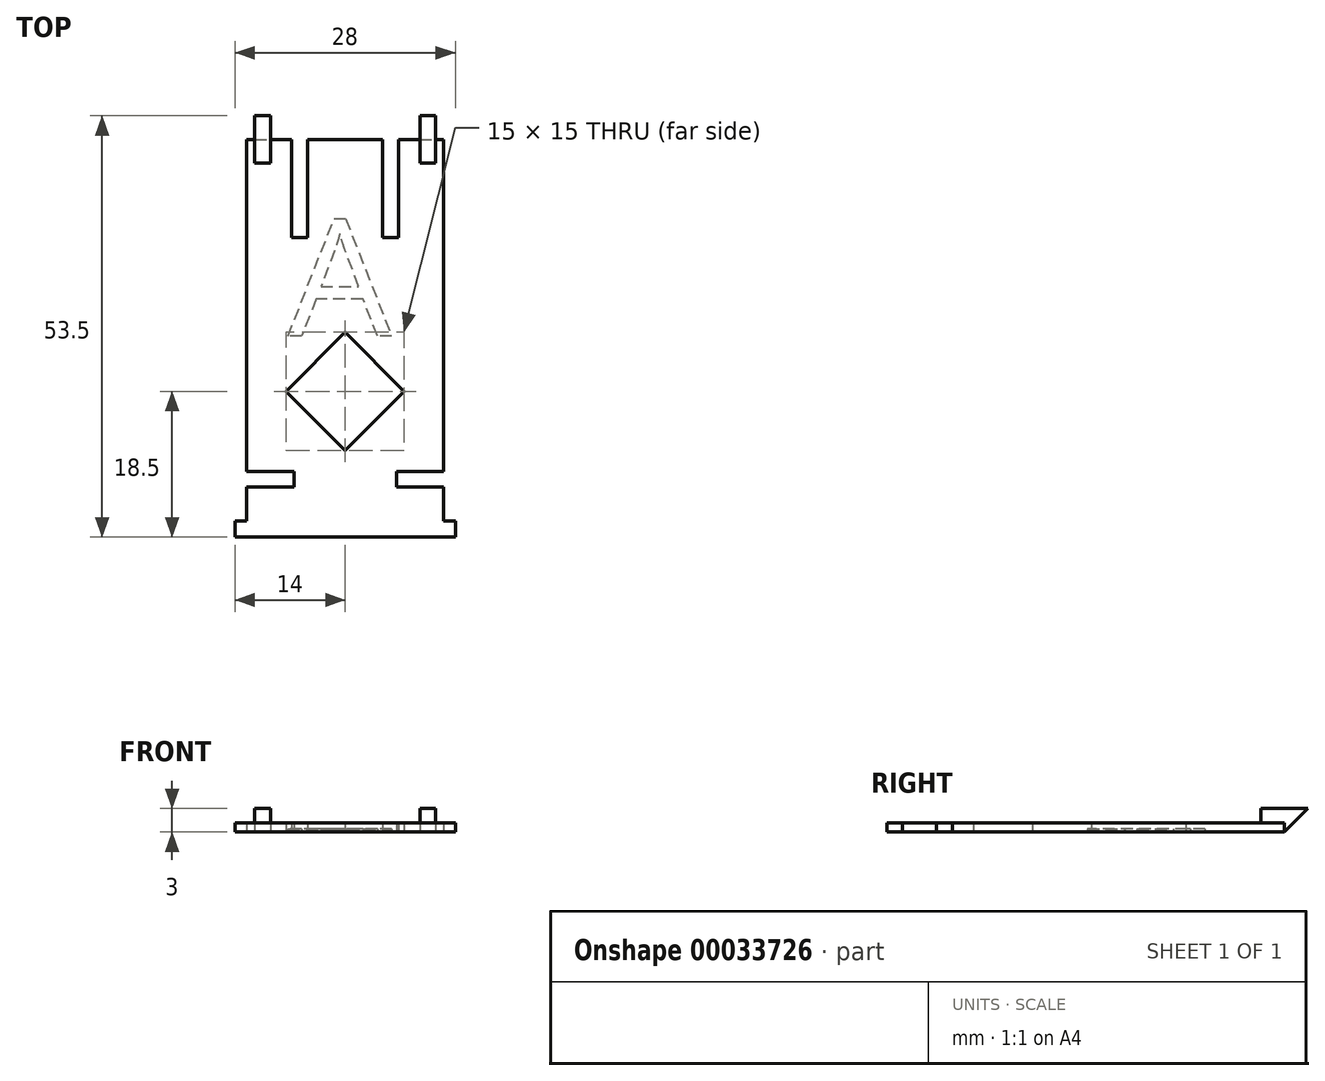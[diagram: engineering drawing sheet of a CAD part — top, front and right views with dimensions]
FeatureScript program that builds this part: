
annotation { "Feature Type Name" : "Feature", "Feature Type Description" : "" }
export const myFeature = defineFeature(function(context is Context, id is Id, definition is map)
    precondition{}
    {
        {
            var Q0;
            Q0=qCreatedBy(makeId("Top.planeOp"),FACE);
            var sketch = newSketch(context, id + "F0", { "sketchPlane" : qUnion([Q0])});
            skLineSegment(sketch, "E0.bottom", {"start": v(-12.5, 25.25) * mm, "end": v(12.5, 25.25) * mm});
            skLineSegment(sketch, "E0.top", {"start": v(-12.5, -25.25) * mm, "end": v(12.5, -25.25) * mm});
            skLineSegment(sketch, "E0.left", {"start": v(-12.5, 25.25) * mm, "end": v(-12.5, -25.25) * mm});
            skLineSegment(sketch, "E0.right", {"start": v(12.5, 25.25) * mm, "end": v(12.5, -25.25) * mm});
            skPoint(sketch, "E0.middle", {"position": v(0, 0) * mm});
            skLineSegment(sketch, "E1.bottom", {"start": v(-11.5, 28.25) * mm, "end": v(-9.5, 28.25) * mm});
            skLineSegment(sketch, "E1.top", {"start": v(-11.5, 22.25) * mm, "end": v(-9.5, 22.25) * mm});
            skLineSegment(sketch, "E1.left", {"start": v(-11.5, 28.25) * mm, "end": v(-11.5, 22.25) * mm});
            skLineSegment(sketch, "E1.right", {"start": v(-9.5, 28.25) * mm, "end": v(-9.5, 22.25) * mm});
            skPoint(sketch, "E1.middle", {"position": v(-10.5, 25.25) * mm});
            skLineSegment(sketch, "E2.MirrorCS", {"start": v(9.5, 28.25) * mm, "end": v(9.5, 22.25) * mm});
            skLineSegment(sketch, "E3.MirrorCS", {"start": v(11.5, 28.25) * mm, "end": v(9.5, 28.25) * mm});
            skLineSegment(sketch, "E4.MirrorCS", {"start": v(11.5, 28.25) * mm, "end": v(11.5, 22.25) * mm});
            skLineSegment(sketch, "E5.MirrorCS", {"start": v(11.5, 22.25) * mm, "end": v(9.5, 22.25) * mm});
            skPoint(sketch, "E6.MirrorP", {"position": v(10.5, 25.25) * mm});
            skLineSegment(sketch, "E7.bottom", {"start": v(-6.78, 12.75) * mm, "end": v(-4.78, 12.75) * mm});
            skLineSegment(sketch, "E7.top", {"start": v(-6.78, 37.75) * mm, "end": v(-4.78, 37.75) * mm});
            skLineSegment(sketch, "E7.left", {"start": v(-6.78, 12.75) * mm, "end": v(-6.78, 37.75) * mm});
            skLineSegment(sketch, "E7.right", {"start": v(-4.78, 12.75) * mm, "end": v(-4.78, 37.75) * mm});
            skPoint(sketch, "E7.middle", {"position": v(-5.78, 25.25) * mm});
            skLineSegment(sketch, "E8.MirrorCS", {"start": v(6.78, 12.75) * mm, "end": v(6.78, 37.75) * mm});
            skLineSegment(sketch, "E9.MirrorCS", {"start": v(4.78, 12.75) * mm, "end": v(4.78, 37.75) * mm});
            skLineSegment(sketch, "E10.MirrorCS", {"start": v(6.78, 37.75) * mm, "end": v(4.78, 37.75) * mm});
            skLineSegment(sketch, "E11.MirrorCS", {"start": v(6.78, 12.75) * mm, "end": v(4.78, 12.75) * mm});
            skCircle(sketch, "E12.cCircle", {"center": v(0, -6.75) * mm, "radius": 7.5 * mm, "construction": true});
            skLineSegment(sketch, "E12.0", {"start": v(0, 0.75) * mm, "end": v(7.5, -6.75) * mm});
            skLineSegment(sketch, "E12.1", {"start": v(7.5, -6.75) * mm, "end": v(0, -14.25) * mm});
            skLineSegment(sketch, "E12.2", {"start": v(0, -14.25) * mm, "end": v(-7.5, -6.75) * mm});
            skLineSegment(sketch, "E12.3", {"start": v(-7.5, -6.75) * mm, "end": v(0, 0.75) * mm});
            skLineSegment(sketch, "E13.bottom", {"start": v(-12.5, -25.25) * mm, "end": v(-14, -25.25) * mm});
            skLineSegment(sketch, "E13.top", {"start": v(-12.5, -23.25) * mm, "end": v(-14, -23.25) * mm});
            skLineSegment(sketch, "E13.left", {"start": v(-12.5, -25.25) * mm, "end": v(-12.5, -23.25) * mm});
            skLineSegment(sketch, "E13.right", {"start": v(-14, -25.25) * mm, "end": v(-14, -23.25) * mm});
            skLineSegment(sketch, "E14.MirrorCS", {"start": v(14, -25.25) * mm, "end": v(14, -23.25) * mm});
            skLineSegment(sketch, "E15.MirrorCS", {"start": v(12.5, -23.25) * mm, "end": v(14, -23.25) * mm});
            skLineSegment(sketch, "E16.MirrorCS", {"start": v(12.5, -25.25) * mm, "end": v(14, -25.25) * mm});
            skLineSegment(sketch, "E17.bottom", {"start": v(-18.5, -16.93) * mm, "end": v(-6.5, -16.93) * mm});
            skLineSegment(sketch, "E17.top", {"start": v(-18.5, -18.93) * mm, "end": v(-6.5, -18.93) * mm});
            skLineSegment(sketch, "E17.left", {"start": v(-18.5, -16.93) * mm, "end": v(-18.5, -18.93) * mm});
            skLineSegment(sketch, "E17.right", {"start": v(-6.5, -16.93) * mm, "end": v(-6.5, -18.93) * mm});
            skPoint(sketch, "E17.middle", {"position": v(-12.5, -17.93) * mm});
            skLineSegment(sketch, "E18.MirrorCS", {"start": v(18.5, -16.93) * mm, "end": v(6.5, -16.93) * mm});
            skLineSegment(sketch, "E19.MirrorCS", {"start": v(18.5, -18.93) * mm, "end": v(6.5, -18.93) * mm});
            skLineSegment(sketch, "E20.MirrorCS", {"start": v(6.5, -16.93) * mm, "end": v(6.5, -18.93) * mm});
            skLineSegment(sketch, "E21.MirrorCS", {"start": v(18.5, -16.93) * mm, "end": v(18.5, -18.93) * mm});
            skText(sketch, "E22", { "text": "A", "fontName": "OpenSans-Regular.ttf"});
            const initialGuessF0  = {"E22": [-0.00727, 0.00025, 1, 0, 0.015]};
            skSetInitialGuess(sketch, initialGuessF0);
            skSolve(sketch);
        }
        {
            var Q0;
            {var subQ11=sQuery(id+"F0.wireOp",EDGE,"E0.top");Q0=makeQuery(id+"F0.imprint","IMPRINT",FACE,{"disambiguationData":[TD([[makeQuery(id+"F0.imprint","IMPRINT",EDGE,{"derivedFrom":subQ11}),1.0]])]});}
            var Q1;
            {var subQ0=sQuery(id+"F0.wireOp",EDGE,"E13.bottom");Q1=makeQuery(id+"F0.imprint","IMPRINT",FACE,{"disambiguationData":[TD([[makeQuery(id+"F0.imprint","IMPRINT",EDGE,{"derivedFrom":subQ0}),-1.0]])]});}
            var Q2;
            Q2=makeQuery(id+"F0.imprint","IMPRINT",FACE,{"disambiguationData":[TD([[makeQuery(id+"F0.imprint","IMPRINT",EDGE,{"derivedFrom":sQuery(id+"F0.wireOp",EDGE,"E14.MirrorCS")}),1.0]])]});
            var Q3;
            {var subQ5=sQuery(id+"F0.wireOp",EDGE,"E1.top");Q3=makeQuery(id+"F0.imprint","IMPRINT",FACE,{"disambiguationData":[TD([[makeQuery(id+"F0.imprint","IMPRINT",EDGE,{"derivedFrom":subQ5}),1.0]])]});}
            var Q4;
            {var subQ5=sQuery(id+"F0.wireOp",EDGE,"E1.bottom");Q4=makeQuery(id+"F0.imprint","IMPRINT",FACE,{"disambiguationData":[TD([[makeQuery(id+"F0.imprint","IMPRINT",EDGE,{"derivedFrom":subQ5}),-1.0]])]});}
            var Q5;
            {var subQ5=sQuery(id+"F0.wireOp",EDGE,"E3.MirrorCS");Q5=makeQuery(id+"F0.imprint","IMPRINT",FACE,{"disambiguationData":[TD([[makeQuery(id+"F0.imprint","IMPRINT",EDGE,{"derivedFrom":subQ5}),1.0]])]});}
            var Q6;
            {var subQ5=sQuery(id+"F0.wireOp",EDGE,"E5.MirrorCS");Q6=makeQuery(id+"F0.imprint","IMPRINT",FACE,{"disambiguationData":[TD([[makeQuery(id+"F0.imprint","IMPRINT",EDGE,{"derivedFrom":subQ5}),-1.0]])]});}
            var Q7;
            Q7=makeQuery(id+"F0.imprint","IMPRINT",FACE,{"disambiguationData":[TD([[makeQuery(id+"F0.imprint","IMPRINT",EDGE,{"derivedFrom":sQuery(id+"F0.wireOp",EDGE,"E22.sketch_text.stroke-0")}),-1.0]])]});
            var Q8;
            Q8=makeQuery(id+"F0.imprint","IMPRINT",FACE,{"disambiguationData":[TD([[makeQuery(id+"F0.imprint","IMPRINT",EDGE,{"derivedFrom":sQuery(id+"F0.wireOp",EDGE,"E22.sketch_text.stroke-8")}),1.0]])]});
            extrude(context, id + "F1", {"entities" : qUnion([Q0, Q1, Q2, Q3, Q4, Q5, Q6, Q7, Q8]), "depth" : 1.2 * mm, "offsetDistance" : 25 * mm});
        }
        {
            var Q0;
            {var subQ5=sQuery(id+"F0.wireOp",EDGE,"E3.MirrorCS");Q0=makeQuery(id+"F0.imprint","IMPRINT",FACE,{"disambiguationData":[TD([[makeQuery(id+"F0.imprint","IMPRINT",EDGE,{"derivedFrom":subQ5}),1.0]])]});}
            var Q1;
            {var subQ5=sQuery(id+"F0.wireOp",EDGE,"E1.bottom");Q1=makeQuery(id+"F0.imprint","IMPRINT",FACE,{"disambiguationData":[TD([[makeQuery(id+"F0.imprint","IMPRINT",EDGE,{"derivedFrom":subQ5}),-1.0]])]});}
            var Q2;
            {var subQ5=sQuery(id+"F0.wireOp",EDGE,"E5.MirrorCS");Q2=makeQuery(id+"F0.imprint","IMPRINT",FACE,{"disambiguationData":[TD([[makeQuery(id+"F0.imprint","IMPRINT",EDGE,{"derivedFrom":subQ5}),-1.0]])]});}
            var Q3;
            {var subQ5=sQuery(id+"F0.wireOp",EDGE,"E1.top");Q3=makeQuery(id+"F0.imprint","IMPRINT",FACE,{"disambiguationData":[TD([[makeQuery(id+"F0.imprint","IMPRINT",EDGE,{"derivedFrom":subQ5}),1.0]])]});}
            extrude(context, id + "F2", {"entities" : qUnion([Q0, Q1, Q2, Q3]), "operationType" : NewBodyOperationType.ADD, "depth" : 3 * mm, "offsetDistance" : 25 * mm});
        }
        {
            var Q0;
            Q0=makeQuery(id+"F1.opExtrude","CAP_EDGE",EDGE,{"disambiguationData":[OSD([sQuery(id+"F0.wireOp",EDGE,"E1.bottom")])],"isStart":true});
            var Q1;
            Q1=makeQuery(id+"F1.opExtrude","CAP_EDGE",EDGE,{"disambiguationData":[OSD([sQuery(id+"F0.wireOp",EDGE,"E3.MirrorCS")])],"isStart":true});
            chamfer(context, id + "F3", {"entities" : qUnion([Q0, Q1]), "width" : 3 * mm, "tangentPropagation" : true});
        }
        {
            var Q0;
            Q0=makeQuery(id+"F0.imprint","IMPRINT",FACE,{"disambiguationData":[TD([[makeQuery(id+"F0.imprint","IMPRINT",EDGE,{"derivedFrom":sQuery(id+"F0.wireOp",EDGE,"E22.sketch_text.stroke-0")}),-1.0]])]});
            extrude(context, id + "F4", {"entities" : qUnion([Q0]), "operationType" : NewBodyOperationType.REMOVE, "depth" : 0.4 * mm, "offsetDistance" : 25 * mm});
        }
        {
            var Q0;
            Q0=makeQuery(id+"F0.imprint","IMPRINT",FACE,{"disambiguationData":[TD([[makeQuery(id+"F0.imprint","IMPRINT",EDGE,{"derivedFrom":sQuery(id+"F0.wireOp",EDGE,"E22.sketch_text.stroke-8")}),1.0]])]});
            extrude(context, id + "F5", {"entities" : qUnion([Q0]), "operationType" : NewBodyOperationType.ADD, "depth" : 1.2 * mm, "offsetDistance" : 25 * mm});
        }
    });
